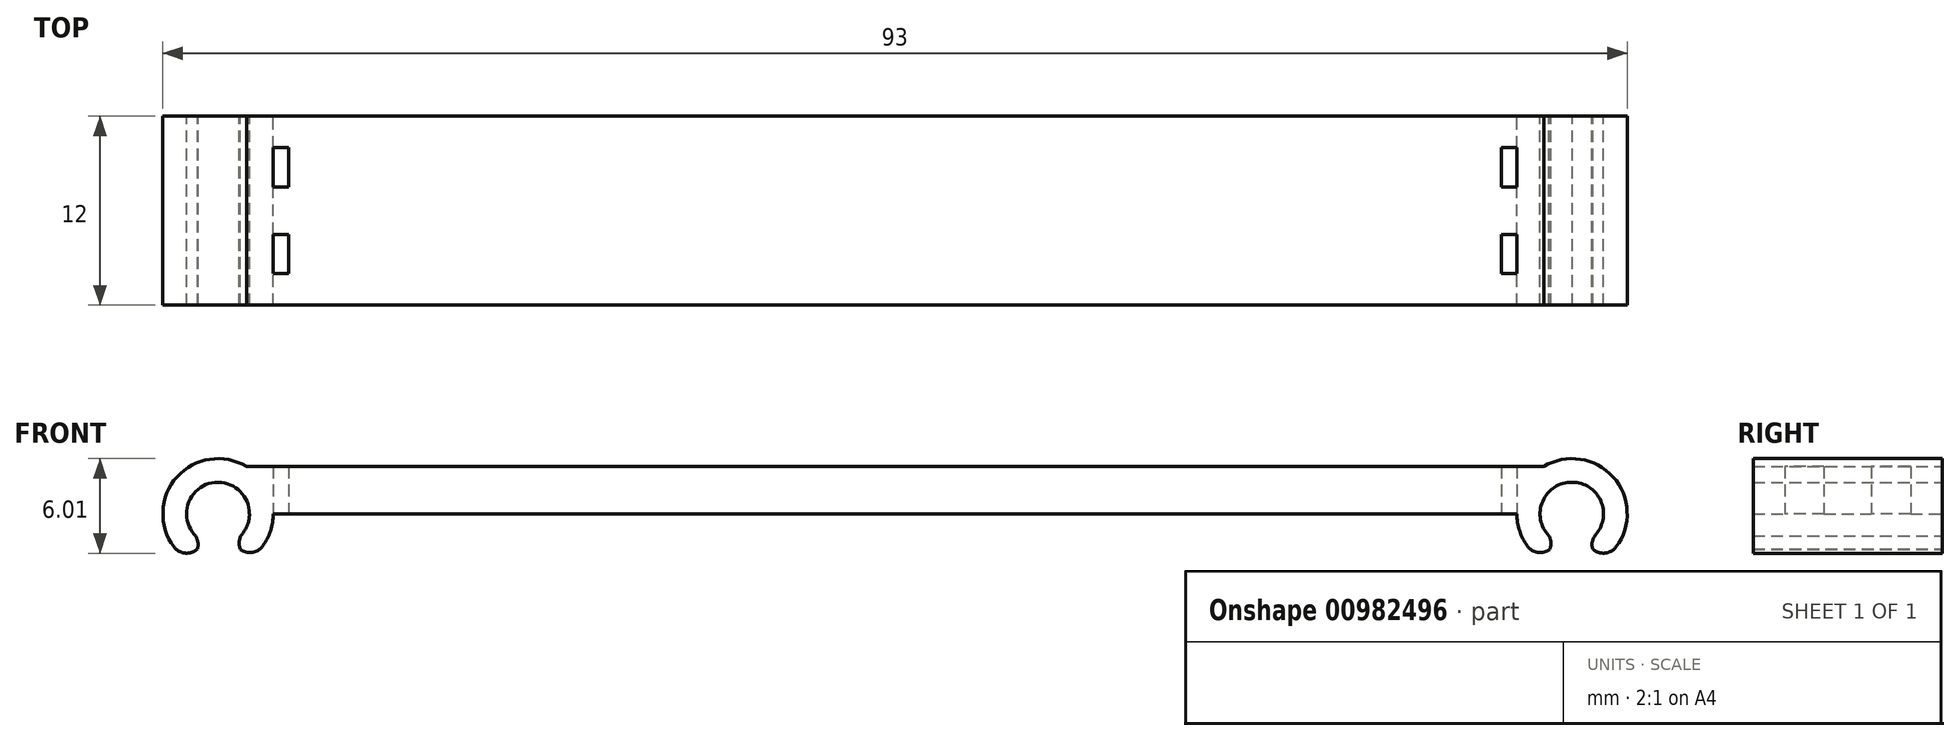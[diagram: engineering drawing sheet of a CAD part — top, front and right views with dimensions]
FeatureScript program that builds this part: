
annotation { "Feature Type Name" : "Feature", "Feature Type Description" : "" }
export const myFeature = defineFeature(function(context is Context, id is Id, definition is map)
    precondition{}
    {
        {
            var Q0;
            Q0=qCreatedBy(makeId("Front.planeOp"),FACE);
            var sketch = newSketch(context, id + "F0", { "sketchPlane" : qUnion([Q0])});
            skLineSegment(sketch, "E0", {"start": v(-43, 0) * mm, "end": v(43, 0) * mm});
            skCircle(sketch, "E1", {"center": v(-43, 0) * mm, "radius": 2 * mm});
            skCircle(sketch, "E2", {"center": v(-43, 0) * mm, "radius": 3.5 * mm});
            skLineSegment(sketch, "E3", {"start": v(-43.97, -1.75) * mm, "end": v(-44.75, -3.03) * mm});
            skLineSegment(sketch, "E4", {"start": v(-42.03, -1.75) * mm, "end": v(-41.1, -2.94) * mm});
            skLineSegment(sketch, "E5.MirrorCS", {"start": v(42.03, -1.75) * mm, "end": v(41.1, -2.94) * mm});
            skLineSegment(sketch, "E6.MirrorCS", {"start": v(43, 0) * mm, "end": v(-43, 0) * mm});
            skLineSegment(sketch, "E7.MirrorCS", {"start": v(43.97, -1.75) * mm, "end": v(44.75, -3.03) * mm});
            skCircle(sketch, "E8.MirrorC", {"center": v(43, 0) * mm, "radius": 2 * mm});
            skCircle(sketch, "E9.MirrorC", {"center": v(43, 0) * mm, "radius": 3.5 * mm});
            skSolve(sketch);
        }
        {
            var Q0;
            {var subQ0=sQuery(id+"F0.wireOp",EDGE,"E3");Q0=makeQuery(id+"F0.imprint","IMPRINT",FACE,{"disambiguationData":[TD([[makeQuery(id+"F0.imprint","IMPRINT",EDGE,{"derivedFrom":subQ0}),-1.0]])]});}
            var Q1;
            {var subQ0=sQuery(id+"F0.wireOp",EDGE,"E4");Q1=makeQuery(id+"F0.imprint","IMPRINT",FACE,{"disambiguationData":[TD([[makeQuery(id+"F0.imprint","IMPRINT",EDGE,{"derivedFrom":subQ0}),1.0]])]});}
            var Q2;
            {var subQ0=sQuery(id+"F0.wireOp",EDGE,"E5.MirrorCS");Q2=makeQuery(id+"F0.imprint","IMPRINT",FACE,{"disambiguationData":[TD([[makeQuery(id+"F0.imprint","IMPRINT",EDGE,{"derivedFrom":subQ0}),-1.0]])]});}
            var Q3;
            {var subQ5=sQuery(id+"F0.wireOp",EDGE,"E7.MirrorCS");Q3=makeQuery(id+"F0.imprint","IMPRINT",FACE,{"disambiguationData":[TD([[makeQuery(id+"F0.imprint","IMPRINT",EDGE,{"derivedFrom":subQ5}),1.0]])]});}
            extrude(context, id + "F1", {"entities" : qUnion([Q0, Q1, Q2, Q3]), "depth" : 12 * mm, "offsetDistance" : 25 * mm});
        }
        {
            var Q0;
            Q0=makeQuery(id+"F1.opExtrude","SWEPT_EDGE",EDGE,{"disambiguationData":[OSD([sQuery(id+"F0.wireOp",EDGE,"E5.MirrorCS"),sQuery(id+"F0.wireOp",EDGE,"E8.MirrorC")])]});
            var Q1;
            Q1=makeQuery(id+"F1.opExtrude","SWEPT_EDGE",EDGE,{"disambiguationData":[OSD([sQuery(id+"F0.wireOp",EDGE,"E7.MirrorCS"),sQuery(id+"F0.wireOp",EDGE,"E8.MirrorC")])]});
            var Q2;
            Q2=makeQuery(id+"F1.opExtrude","SWEPT_EDGE",EDGE,{"disambiguationData":[OSD([sQuery(id+"F0.wireOp",EDGE,"E1"),sQuery(id+"F0.wireOp",EDGE,"E4")])]});
            var Q3;
            Q3=makeQuery(id+"F1.opExtrude","SWEPT_EDGE",EDGE,{"disambiguationData":[OSD([sQuery(id+"F0.wireOp",EDGE,"E1"),sQuery(id+"F0.wireOp",EDGE,"E3")])]});
            var Q4;
            Q4=makeQuery(id+"F1.opExtrude","SWEPT_EDGE",EDGE,{"disambiguationData":[OSD([sQuery(id+"F0.wireOp",EDGE,"E2"),sQuery(id+"F0.wireOp",EDGE,"E4")])]});
            var Q5;
            Q5=makeQuery(id+"F1.opExtrude","SWEPT_EDGE",EDGE,{"disambiguationData":[OSD([sQuery(id+"F0.wireOp",EDGE,"E2"),sQuery(id+"F0.wireOp",EDGE,"E3")])]});
            var Q6;
            Q6=makeQuery(id+"F1.opExtrude","SWEPT_EDGE",EDGE,{"disambiguationData":[OSD([sQuery(id+"F0.wireOp",EDGE,"E5.MirrorCS"),sQuery(id+"F0.wireOp",EDGE,"E9.MirrorC")])]});
            var Q7;
            Q7=makeQuery(id+"F1.opExtrude","SWEPT_EDGE",EDGE,{"disambiguationData":[OSD([sQuery(id+"F0.wireOp",EDGE,"E7.MirrorCS"),sQuery(id+"F0.wireOp",EDGE,"E9.MirrorC")])]});
            fillet(context, id + "F2", {"entities" : qUnion([Q0, Q1, Q2, Q3, Q4, Q5, Q6, Q7]), "radius" : 1 * mm, "tangentPropagation" : true, "allowEdgeOverflow" : false});
        }
        {
            var Q0;
            Q0=qCreatedBy(makeId("Top.planeOp"),FACE);
            var sketch = newSketch(context, id + "F3", { "sketchPlane" : qUnion([Q0])});
            skLineSegment(sketch, "E10.bottom", {"start": v(-42.99, 0) * mm, "end": v(43.01, 0) * mm});
            skLineSegment(sketch, "E10.top", {"start": v(-42.99, -12) * mm, "end": v(43.01, -12) * mm});
            skLineSegment(sketch, "E10.left", {"start": v(-42.99, 0) * mm, "end": v(-42.99, -12) * mm});
            skLineSegment(sketch, "E10.right", {"start": v(43.01, 0) * mm, "end": v(43.01, -12) * mm});
            skSolve(sketch);
        }
        {
            var Q0;
            Q0=makeQuery(id+"F3.imprint","IMPRINT",FACE,{"disambiguationData":[TD([[makeQuery(id+"F3.imprint","IMPRINT",EDGE,{"derivedFrom":sQuery(id+"F3.wireOp",EDGE,"E10.bottom")}),-1.0]])]});
            extrude(context, id + "F4", {"entities" : qUnion([Q0]), "depth" : 3 * mm, "offsetDistance" : 25 * mm});
        }
        {
            var Q0;
            Q0=makeQuery(id+"F4.opExtrude","SWEPT_BODY",BODY,{"disambiguationData":[OSD([sQuery(id+"F3.wireOp",EDGE,"E10.bottom"),sQuery(id+"F3.wireOp",EDGE,"E10.top"),sQuery(id+"F3.wireOp",EDGE,"E10.left"),sQuery(id+"F3.wireOp",EDGE,"E10.right")])]});
            var Q1;
            Q1=makeQuery(id+"F1.opExtrude","SWEPT_BODY",BODY,{"disambiguationData":[OSD([sQuery(id+"F0.wireOp",EDGE,"E5.MirrorCS"),sQuery(id+"F0.wireOp",EDGE,"E7.MirrorCS"),sQuery(id+"F0.wireOp",EDGE,"E8.MirrorC"),sQuery(id+"F0.wireOp",EDGE,"E9.MirrorC")])]});
            booleanBodies(context, id + "F5", {"operationType" : BooleanOperationType.UNION, "tools" : qUnion([Q0, Q1])});
        }
        {
            var Q0;
            Q0=makeQuery(id+"F1.opExtrude","SWEPT_BODY",BODY,{"disambiguationData":[OSD([sQuery(id+"F0.wireOp",EDGE,"E1"),sQuery(id+"F0.wireOp",EDGE,"E2"),sQuery(id+"F0.wireOp",EDGE,"E3"),sQuery(id+"F0.wireOp",EDGE,"E4")])]});
            var Q1;
            Q1=makeQuery(id+"F4.opExtrude","SWEPT_BODY",BODY,{"disambiguationData":[OSD([sQuery(id+"F3.wireOp",EDGE,"E10.bottom"),sQuery(id+"F3.wireOp",EDGE,"E10.top"),sQuery(id+"F3.wireOp",EDGE,"E10.left"),sQuery(id+"F3.wireOp",EDGE,"E10.right")])]});
            booleanBodies(context, id + "F6", {"operationType" : BooleanOperationType.UNION, "tools" : qUnion([Q0, Q1])});
        }
        {
            var Q0;
            Q0=qCreatedBy(makeId("Front.planeOp"),FACE);
            var sketch = newSketch(context, id + "F7", { "sketchPlane" : qUnion([Q0])});
            skCircle(sketch, "E11", {"center": v(42.97, 0) * mm, "radius": 2 * mm});
            skCircle(sketch, "E12", {"center": v(-43, 0) * mm, "radius": 2 * mm});
            skSolve(sketch);
        }
        {
            var Q0;
            Q0=makeQuery(id+"F7.imprint","IMPRINT",FACE,{"disambiguationData":[TD([[makeQuery(id+"F7.imprint","IMPRINT",EDGE,{"derivedFrom":sQuery(id+"F7.wireOp",EDGE,"E12")}),1.0]])]});
            var Q1;
            Q1=makeQuery(id+"F7.imprint","IMPRINT",FACE,{"disambiguationData":[TD([[makeQuery(id+"F7.imprint","IMPRINT",EDGE,{"derivedFrom":sQuery(id+"F7.wireOp",EDGE,"E11")}),1.0]])]});
            extrude(context, id + "F8", {"entities" : qUnion([Q0, Q1]), "operationType" : NewBodyOperationType.REMOVE, "depth" : 25 * mm, "offsetDistance" : 25 * mm});
        }
        {
            var Q0;
            {var subQ0=sQuery(id+"F0.wireOp",EDGE,"E2");var subQ1=sQuery(id+"F0.wireOp",EDGE,"E9.MirrorC");var subQ10=sQuery(id+"F3.wireOp",EDGE,"E10.top");var subQ12=makeQuery(id+"F1.opExtrude","SWEPT_FACE",FACE,{"disambiguationData":[OSD([subQ1])]});var subQ13=sQuery(id+"F3.wireOp",EDGE,"E10.bottom");var subQ15=sQuery(id+"F3.wireOp",EDGE,"E10.left");Q0=makeQuery(id+"F6.opBoolean","SPLIT",FACE,{"disambiguationData":[TD([makeQuery(id+"F1.opExtrude","SWEPT_FACE",FACE,{"disambiguationData":[OSD([subQ0])]})])],"derivedFrom":makeQuery(id+"F5.opBoolean","SPLIT",FACE,{"disambiguationData":[TD([subQ12])],"derivedFrom":makeQuery(id+"F4.opExtrude","CAP_FACE",FACE,{"disambiguationData":[OSD([subQ13,subQ10,subQ15,sQuery(id+"F3.wireOp",EDGE,"E10.right")])],"isStart":true})})});}
            var sketch = newSketch(context, id + "F9", { "sketchPlane" : qUnion([Q0])});
            skLineSegment(sketch, "E13.bottom", {"start": v(39.5, 2) * mm, "end": v(38.5, 2) * mm});
            skLineSegment(sketch, "E13.top", {"start": v(39.5, 4.5) * mm, "end": v(38.5, 4.5) * mm});
            skLineSegment(sketch, "E13.left", {"start": v(39.5, 2) * mm, "end": v(39.5, 4.5) * mm});
            skLineSegment(sketch, "E13.right", {"start": v(38.5, 2) * mm, "end": v(38.5, 4.5) * mm});
            skLineSegment(sketch, "E14.MirrorCS", {"start": v(-39.5, 2) * mm, "end": v(-38.5, 2) * mm});
            skLineSegment(sketch, "E15.MirrorCS", {"start": v(-38.5, 2) * mm, "end": v(-38.5, 4.5) * mm});
            skLineSegment(sketch, "E16.MirrorCS", {"start": v(-39.5, 2) * mm, "end": v(-39.5, 4.5) * mm});
            skLineSegment(sketch, "E17.MirrorCS", {"start": v(-39.5, 4.5) * mm, "end": v(-38.5, 4.5) * mm});
            skLineSegment(sketch, "E18.bottom", {"start": v(39.5, 7.5) * mm, "end": v(38.5, 7.5) * mm});
            skLineSegment(sketch, "E18.top", {"start": v(39.5, 10) * mm, "end": v(38.5, 10) * mm});
            skLineSegment(sketch, "E18.left", {"start": v(39.5, 7.5) * mm, "end": v(39.5, 10) * mm});
            skLineSegment(sketch, "E18.right", {"start": v(38.5, 7.5) * mm, "end": v(38.5, 10) * mm});
            skLineSegment(sketch, "E19.bottom", {"start": v(-39.5, 10) * mm, "end": v(-38.5, 10) * mm});
            skLineSegment(sketch, "E19.top", {"start": v(-39.5, 7.5) * mm, "end": v(-38.5, 7.5) * mm});
            skLineSegment(sketch, "E19.left", {"start": v(-39.5, 10) * mm, "end": v(-39.5, 7.5) * mm});
            skLineSegment(sketch, "E19.right", {"start": v(-38.5, 10) * mm, "end": v(-38.5, 7.5) * mm});
            skSolve(sketch);
        }
        {
            var Q0;
            Q0=makeQuery(id+"F9.imprint","IMPRINT",FACE,{"disambiguationData":[TD([[makeQuery(id+"F9.imprint","IMPRINT",EDGE,{"derivedFrom":sQuery(id+"F9.wireOp",EDGE,"E13.bottom")}),-1.0]])]});
            var Q1;
            Q1=makeQuery(id+"F9.imprint","IMPRINT",FACE,{"disambiguationData":[TD([[makeQuery(id+"F9.imprint","IMPRINT",EDGE,{"derivedFrom":sQuery(id+"F9.wireOp",EDGE,"E14.MirrorCS")}),1.0]])]});
            var Q2;
            Q2=makeQuery(id+"F9.imprint","IMPRINT",FACE,{"disambiguationData":[TD([[makeQuery(id+"F9.imprint","IMPRINT",EDGE,{"derivedFrom":sQuery(id+"F9.wireOp",EDGE,"E19.bottom")}),-1.0]])]});
            var Q3;
            Q3=makeQuery(id+"F9.imprint","IMPRINT",FACE,{"disambiguationData":[TD([[makeQuery(id+"F9.imprint","IMPRINT",EDGE,{"derivedFrom":sQuery(id+"F9.wireOp",EDGE,"E18.bottom")}),-1.0]])]});
            extrude(context, id + "F10", {"entities" : qUnion([Q0, Q1, Q2, Q3]), "operationType" : NewBodyOperationType.REMOVE, "oppositeDirection" : true, "depth" : 25 * mm, "offsetDistance" : 25 * mm});
        }
    });
